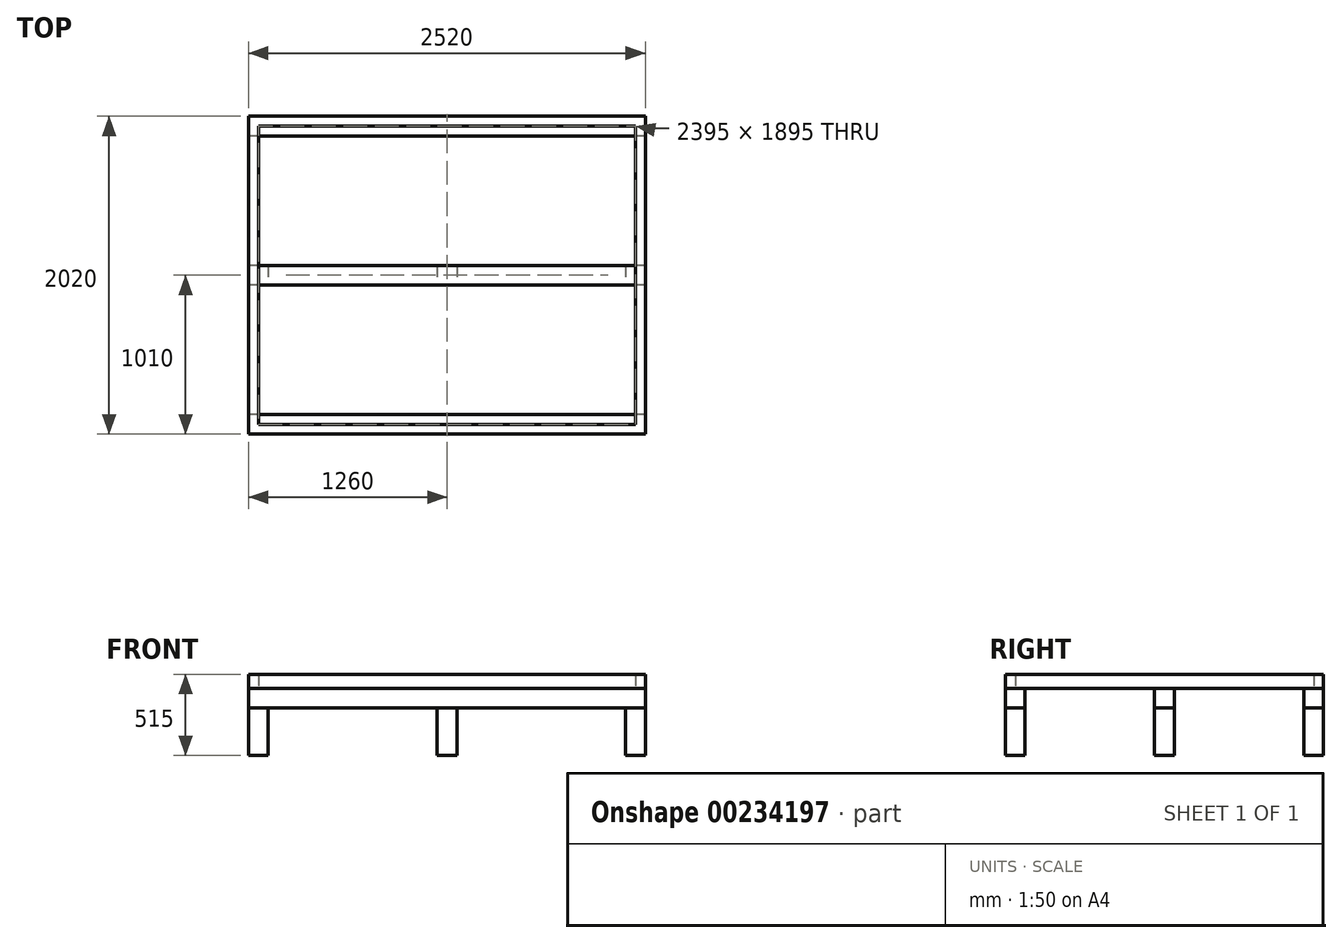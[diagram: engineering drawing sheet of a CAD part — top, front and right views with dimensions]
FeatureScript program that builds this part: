
annotation { "Feature Type Name" : "Feature", "Feature Type Description" : "" }
export const myFeature = defineFeature(function(context is Context, id is Id, definition is map)
    precondition{}
    {
        {
            var Q0;
            Q0=qCreatedBy(makeId("Top.planeOp"),FACE);
            var sketch = newSketch(context, id + "F0", { "sketchPlane" : qUnion([Q0])});
            skLineSegment(sketch, "E0.bottom", {"start": v(-1260, 1010) * mm, "end": v(-1135, 1010) * mm});
            skLineSegment(sketch, "E0.top", {"start": v(-1260, 885) * mm, "end": v(-1135, 885) * mm});
            skLineSegment(sketch, "E0.left", {"start": v(-1260, 1010) * mm, "end": v(-1260, 885) * mm});
            skLineSegment(sketch, "E0.right", {"start": v(-1135, 1010) * mm, "end": v(-1135, 885) * mm});
            skLineSegment(sketch, "E1.bottom", {"start": v(1260, -1010) * mm, "end": v(-1260, -1010) * mm, "construction": true});
            skLineSegment(sketch, "E1.top", {"start": v(1260, 1010) * mm, "end": v(-1260, 1010) * mm, "construction": true});
            skLineSegment(sketch, "E1.left", {"start": v(1260, -1010) * mm, "end": v(1260, 1010) * mm, "construction": true});
            skLineSegment(sketch, "E1.right", {"start": v(-1260, -1010) * mm, "end": v(-1260, 1010) * mm, "construction": true});
            skPoint(sketch, "E1.middle", {"position": v(0, 0) * mm});
            skLineSegment(sketch, "E2.0.1.0", {"start": v(-1135, 62.5) * mm, "end": v(-1135, -62.5) * mm});
            skLineSegment(sketch, "E2.0.1.1", {"start": v(-1260, 62.5) * mm, "end": v(-1260, -62.5) * mm});
            skLineSegment(sketch, "E2.0.1.2", {"start": v(-1260, -62.5) * mm, "end": v(-1135, -62.5) * mm});
            skLineSegment(sketch, "E2.0.1.3", {"start": v(-1260, 62.5) * mm, "end": v(-1135, 62.5) * mm});
            skLineSegment(sketch, "E2.0.2.0", {"start": v(-1135, -885) * mm, "end": v(-1135, -1010) * mm});
            skLineSegment(sketch, "E2.0.2.1", {"start": v(-1260, -885) * mm, "end": v(-1260, -1010) * mm});
            skLineSegment(sketch, "E2.0.2.2", {"start": v(-1260, -1010) * mm, "end": v(-1135, -1010) * mm});
            skLineSegment(sketch, "E2.0.2.3", {"start": v(-1260, -885) * mm, "end": v(-1135, -885) * mm});
            skLineSegment(sketch, "E2.1.0.0", {"start": v(62.5, 1010) * mm, "end": v(62.5, 885) * mm});
            skLineSegment(sketch, "E2.1.0.1", {"start": v(-62.5, 1010) * mm, "end": v(-62.5, 885) * mm});
            skLineSegment(sketch, "E2.1.0.2", {"start": v(-62.5, 885) * mm, "end": v(62.5, 885) * mm});
            skLineSegment(sketch, "E2.1.0.3", {"start": v(-62.5, 1010) * mm, "end": v(62.5, 1010) * mm});
            skLineSegment(sketch, "E2.1.1.0", {"start": v(62.5, 62.5) * mm, "end": v(62.5, -62.5) * mm});
            skLineSegment(sketch, "E2.1.1.1", {"start": v(-62.5, 62.5) * mm, "end": v(-62.5, -62.5) * mm});
            skLineSegment(sketch, "E2.1.1.2", {"start": v(-62.5, -62.5) * mm, "end": v(62.5, -62.5) * mm});
            skLineSegment(sketch, "E2.1.1.3", {"start": v(-62.5, 62.5) * mm, "end": v(62.5, 62.5) * mm});
            skLineSegment(sketch, "E2.1.2.0", {"start": v(62.5, -885) * mm, "end": v(62.5, -1010) * mm});
            skLineSegment(sketch, "E2.1.2.1", {"start": v(-62.5, -885) * mm, "end": v(-62.5, -1010) * mm});
            skLineSegment(sketch, "E2.1.2.2", {"start": v(-62.5, -1010) * mm, "end": v(62.5, -1010) * mm});
            skLineSegment(sketch, "E2.1.2.3", {"start": v(-62.5, -885) * mm, "end": v(62.5, -885) * mm});
            skLineSegment(sketch, "E2.2.0.0", {"start": v(1260, 1010) * mm, "end": v(1260, 885) * mm});
            skLineSegment(sketch, "E2.2.0.1", {"start": v(1135, 1010) * mm, "end": v(1135, 885) * mm});
            skLineSegment(sketch, "E2.2.0.2", {"start": v(1135, 885) * mm, "end": v(1260, 885) * mm});
            skLineSegment(sketch, "E2.2.0.3", {"start": v(1135, 1010) * mm, "end": v(1260, 1010) * mm});
            skLineSegment(sketch, "E2.2.1.0", {"start": v(1260, 62.5) * mm, "end": v(1260, -62.5) * mm});
            skLineSegment(sketch, "E2.2.1.1", {"start": v(1135, 62.5) * mm, "end": v(1135, -62.5) * mm});
            skLineSegment(sketch, "E2.2.1.2", {"start": v(1135, -62.5) * mm, "end": v(1260, -62.5) * mm});
            skLineSegment(sketch, "E2.2.1.3", {"start": v(1135, 62.5) * mm, "end": v(1260, 62.5) * mm});
            skLineSegment(sketch, "E2.2.2.0", {"start": v(1260, -885) * mm, "end": v(1260, -1010) * mm});
            skLineSegment(sketch, "E2.2.2.1", {"start": v(1135, -885) * mm, "end": v(1135, -1010) * mm});
            skLineSegment(sketch, "E2.2.2.2", {"start": v(1135, -1010) * mm, "end": v(1260, -1010) * mm});
            skLineSegment(sketch, "E2.2.2.3", {"start": v(1135, -885) * mm, "end": v(1260, -885) * mm});
            skLineSegment(sketch, "E2.direction1", {"start": v(-1260, 885) * mm, "end": v(-62.5, 885) * mm, "construction": true});
            skLineSegment(sketch, "E2.direction2", {"start": v(-1260, 885) * mm, "end": v(-1260, -62.5) * mm, "construction": true});
            skSolve(sketch);
        }
        {
            var Q0;
            Q0 = qSketchRegion(id + "F0", true);
            extrude(context, id + "F1", {"entities" : qUnion([Q0]), "depth" : 300 * mm});
        }
        {
            var Q0;
            Q0=makeQuery(id+"F1.opExtrude","SWEPT_FACE",FACE,{"disambiguationData":[OSD([sQuery(id+"F0.wireOp",EDGE,"E0.left")])]});
            var sketch = newSketch(context, id + "F2", { "sketchPlane" : qUnion([Q0])});
            skLineSegment(sketch, "E3.bottom", {"start": v(-1010, 300) * mm, "end": v(-885, 300) * mm});
            skLineSegment(sketch, "E3.top", {"start": v(-1010, 425) * mm, "end": v(-885, 425) * mm});
            skLineSegment(sketch, "E3.left", {"start": v(-1010, 300) * mm, "end": v(-1010, 425) * mm});
            skLineSegment(sketch, "E3.right", {"start": v(-885, 300) * mm, "end": v(-885, 425) * mm});
            skLineSegment(sketch, "E4.1.0.0", {"start": v(-62.5, 300) * mm, "end": v(62.5, 300) * mm});
            skLineSegment(sketch, "E4.1.0.1", {"start": v(-62.5, 425) * mm, "end": v(62.5, 425) * mm});
            skLineSegment(sketch, "E4.1.0.2", {"start": v(-62.5, 300) * mm, "end": v(-62.5, 425) * mm});
            skLineSegment(sketch, "E4.1.0.3", {"start": v(62.5, 300) * mm, "end": v(62.5, 425) * mm});
            skLineSegment(sketch, "E4.2.0.0", {"start": v(885, 300) * mm, "end": v(1010, 300) * mm});
            skLineSegment(sketch, "E4.2.0.1", {"start": v(885, 425) * mm, "end": v(1010, 425) * mm});
            skLineSegment(sketch, "E4.2.0.2", {"start": v(885, 300) * mm, "end": v(885, 425) * mm});
            skLineSegment(sketch, "E4.2.0.3", {"start": v(1010, 300) * mm, "end": v(1010, 425) * mm});
            skLineSegment(sketch, "E4.direction1", {"start": v(-1010, 300) * mm, "end": v(-62.5, 300) * mm, "construction": true});
            skSolve(sketch);
        }
        {
            var Q0;
            Q0 = qSketchRegion(id + "F2", true);
            var Q1;
            Q1=makeQuery(id+"F1.opExtrude","SWEPT_FACE",FACE,{"disambiguationData":[OSD([sQuery(id+"F0.wireOp",EDGE,"E2.2.2.0")])]});
            extrude(context, id + "F3", {"entities" : qUnion([Q0]), "endBound" : BoundingType.UP_TO_SURFACE, "oppositeDirection" : true, "endBoundEntityFace" : qUnion([Q1]), "depth" : 25 * mm});
        }
        {
            var Q0;
            Q0=makeQuery(id+"F3.opExtrude","SWEPT_FACE",FACE,{"disambiguationData":[OSD([sQuery(id+"F2.wireOp",EDGE,"E3.top")])]});
            var sketch = newSketch(context, id + "F4", { "sketchPlane" : qUnion([Q0])});
            skLineSegment(sketch, "E5.bottom", {"start": v(-1260, 1010) * mm, "end": v(1260, 1010) * mm});
            skLineSegment(sketch, "E5.top", {"start": v(-1260, 947.5) * mm, "end": v(1260, 947.5) * mm});
            skLineSegment(sketch, "E5.left", {"start": v(-1260, 1010) * mm, "end": v(-1260, 947.5) * mm});
            skLineSegment(sketch, "E5.right", {"start": v(1260, 1010) * mm, "end": v(1260, 947.5) * mm});
            skLineSegment(sketch, "E6.bottom", {"start": v(-1260, -1010) * mm, "end": v(1260, -1010) * mm});
            skLineSegment(sketch, "E6.top", {"start": v(-1260, -947.5) * mm, "end": v(1260, -947.5) * mm});
            skLineSegment(sketch, "E6.left", {"start": v(-1260, -1010) * mm, "end": v(-1260, -947.5) * mm});
            skLineSegment(sketch, "E6.right", {"start": v(1260, -1010) * mm, "end": v(1260, -947.5) * mm});
            skLineSegment(sketch, "E7.bottom", {"start": v(-1260, 947.5) * mm, "end": v(-1197.5, 947.5) * mm});
            skLineSegment(sketch, "E7.top", {"start": v(-1260, -947.5) * mm, "end": v(-1197.5, -947.5) * mm});
            skLineSegment(sketch, "E7.left", {"start": v(-1260, 947.5) * mm, "end": v(-1260, -947.5) * mm});
            skLineSegment(sketch, "E7.right", {"start": v(-1197.5, 947.5) * mm, "end": v(-1197.5, -947.5) * mm});
            skLineSegment(sketch, "E8", {"start": v(-1260, 1010) * mm, "end": v(-810, 1010) * mm});
            skLineSegment(sketch, "E9.1.0.0", {"start": v(-787.92, 947.5) * mm, "end": v(-787.92, -947.5) * mm});
            skLineSegment(sketch, "E9.1.0.1", {"start": v(-850.42, 947.5) * mm, "end": v(-850.42, -947.5) * mm});
            skLineSegment(sketch, "E9.1.0.2", {"start": v(-850.42, -947.5) * mm, "end": v(-787.92, -947.5) * mm});
            skLineSegment(sketch, "E9.1.0.3", {"start": v(-850.42, 947.5) * mm, "end": v(-787.92, 947.5) * mm});
            skLineSegment(sketch, "E9.2.0.0", {"start": v(-378.33, 947.5) * mm, "end": v(-378.33, -947.5) * mm});
            skLineSegment(sketch, "E9.2.0.1", {"start": v(-440.83, 947.5) * mm, "end": v(-440.83, -947.5) * mm});
            skLineSegment(sketch, "E9.2.0.2", {"start": v(-440.83, -947.5) * mm, "end": v(-378.33, -947.5) * mm});
            skLineSegment(sketch, "E9.2.0.3", {"start": v(-440.83, 947.5) * mm, "end": v(-378.33, 947.5) * mm});
            skLineSegment(sketch, "E9.3.0.0", {"start": v(31.25, 947.5) * mm, "end": v(31.25, -947.5) * mm});
            skLineSegment(sketch, "E9.3.0.1", {"start": v(-31.25, 947.5) * mm, "end": v(-31.25, -947.5) * mm});
            skLineSegment(sketch, "E9.3.0.2", {"start": v(-31.25, -947.5) * mm, "end": v(31.25, -947.5) * mm});
            skLineSegment(sketch, "E9.3.0.3", {"start": v(-31.25, 947.5) * mm, "end": v(31.25, 947.5) * mm});
            skLineSegment(sketch, "E9.4.0.0", {"start": v(440.83, 947.5) * mm, "end": v(440.83, -947.5) * mm});
            skLineSegment(sketch, "E9.4.0.1", {"start": v(378.33, 947.5) * mm, "end": v(378.33, -947.5) * mm});
            skLineSegment(sketch, "E9.4.0.2", {"start": v(378.33, -947.5) * mm, "end": v(440.83, -947.5) * mm});
            skLineSegment(sketch, "E9.4.0.3", {"start": v(378.33, 947.5) * mm, "end": v(440.83, 947.5) * mm});
            skLineSegment(sketch, "E9.5.0.0", {"start": v(850.42, 947.5) * mm, "end": v(850.42, -947.5) * mm});
            skLineSegment(sketch, "E9.5.0.1", {"start": v(787.92, 947.5) * mm, "end": v(787.92, -947.5) * mm});
            skLineSegment(sketch, "E9.5.0.2", {"start": v(787.92, -947.5) * mm, "end": v(850.42, -947.5) * mm});
            skLineSegment(sketch, "E9.5.0.3", {"start": v(787.92, 947.5) * mm, "end": v(850.42, 947.5) * mm});
            skLineSegment(sketch, "E9.6.0.0", {"start": v(1260, 947.5) * mm, "end": v(1260, -947.5) * mm});
            skLineSegment(sketch, "E9.6.0.1", {"start": v(1197.5, 947.5) * mm, "end": v(1197.5, -947.5) * mm});
            skLineSegment(sketch, "E9.6.0.2", {"start": v(1197.5, -947.5) * mm, "end": v(1260, -947.5) * mm});
            skLineSegment(sketch, "E9.6.0.3", {"start": v(1197.5, 947.5) * mm, "end": v(1260, 947.5) * mm});
            skLineSegment(sketch, "E9.direction1", {"start": v(-1260, -947.5) * mm, "end": v(-850.42, -947.5) * mm, "construction": true});
            skSolve(sketch);
        }
        {
            var Q0;
            Q0 = qSketchRegion(id + "F4", true);
            var Q1;
            {var subQ0=sQuery(id+"F4.wireOp",EDGE,"E9.1.0.2");Q1=makeQuery(id+"F4.imprint","IMPRINT",FACE,{"disambiguationData":[TD([[makeQuery(id+"F4.imprint","IMPRINT",EDGE,{"derivedFrom":subQ0}),1.0]])]});}
            var Q2;
            {var subQ0=sQuery(id+"F4.wireOp",EDGE,"E9.2.0.2");Q2=makeQuery(id+"F4.imprint","IMPRINT",FACE,{"disambiguationData":[TD([[makeQuery(id+"F4.imprint","IMPRINT",EDGE,{"derivedFrom":subQ0}),1.0]])]});}
            var Q3;
            {var subQ0=sQuery(id+"F4.wireOp",EDGE,"E9.3.0.2");Q3=makeQuery(id+"F4.imprint","IMPRINT",FACE,{"disambiguationData":[TD([[makeQuery(id+"F4.imprint","IMPRINT",EDGE,{"derivedFrom":subQ0}),1.0]])]});}
            var Q4;
            {var subQ0=sQuery(id+"F4.wireOp",EDGE,"E9.4.0.2");Q4=makeQuery(id+"F4.imprint","IMPRINT",FACE,{"disambiguationData":[TD([[makeQuery(id+"F4.imprint","IMPRINT",EDGE,{"derivedFrom":subQ0}),1.0]])]});}
            var Q5;
            {var subQ0=sQuery(id+"F4.wireOp",EDGE,"E9.5.0.2");Q5=makeQuery(id+"F4.imprint","IMPRINT",FACE,{"disambiguationData":[TD([[makeQuery(id+"F4.imprint","IMPRINT",EDGE,{"derivedFrom":subQ0}),1.0]])]});}
            var Q6;
            {var subQ0=sQuery(id+"F4.wireOp",EDGE,"E9.6.0.2");Q6=makeQuery(id+"F4.imprint","IMPRINT",FACE,{"disambiguationData":[TD([[makeQuery(id+"F4.imprint","IMPRINT",EDGE,{"derivedFrom":subQ0}),1.0]])]});}
            var Q7;
            {var subQ0=sQuery(id+"F4.wireOp",EDGE,"E9.1.0.3");Q7=makeQuery(id+"F4.imprint","IMPRINT",FACE,{"disambiguationData":[TD([[makeQuery(id+"F4.imprint","IMPRINT",EDGE,{"derivedFrom":subQ0}),-1.0]])]});}
            var Q8;
            {var subQ0=sQuery(id+"F4.wireOp",EDGE,"E9.2.0.3");Q8=makeQuery(id+"F4.imprint","IMPRINT",FACE,{"disambiguationData":[TD([[makeQuery(id+"F4.imprint","IMPRINT",EDGE,{"derivedFrom":subQ0}),-1.0]])]});}
            var Q9;
            {var subQ0=sQuery(id+"F4.wireOp",EDGE,"E9.3.0.3");Q9=makeQuery(id+"F4.imprint","IMPRINT",FACE,{"disambiguationData":[TD([[makeQuery(id+"F4.imprint","IMPRINT",EDGE,{"derivedFrom":subQ0}),-1.0]])]});}
            var Q10;
            {var subQ0=sQuery(id+"F4.wireOp",EDGE,"E9.4.0.3");Q10=makeQuery(id+"F4.imprint","IMPRINT",FACE,{"disambiguationData":[TD([[makeQuery(id+"F4.imprint","IMPRINT",EDGE,{"derivedFrom":subQ0}),-1.0]])]});}
            var Q11;
            {var subQ0=sQuery(id+"F4.wireOp",EDGE,"E9.5.0.3");Q11=makeQuery(id+"F4.imprint","IMPRINT",FACE,{"disambiguationData":[TD([[makeQuery(id+"F4.imprint","IMPRINT",EDGE,{"derivedFrom":subQ0}),-1.0]])]});}
            var Q12;
            {var subQ0=sQuery(id+"F4.wireOp",EDGE,"E9.6.0.3");Q12=makeQuery(id+"F4.imprint","IMPRINT",FACE,{"disambiguationData":[TD([[makeQuery(id+"F4.imprint","IMPRINT",EDGE,{"derivedFrom":subQ0}),-1.0]])]});}
            extrude(context, id + "F5", {"entities" : qUnion([Q0, Q1, Q2, Q3, Q4, Q5, Q6, Q7, Q8, Q9, Q10, Q11, Q12]), "depth" : 90 * mm});
        }
    });
